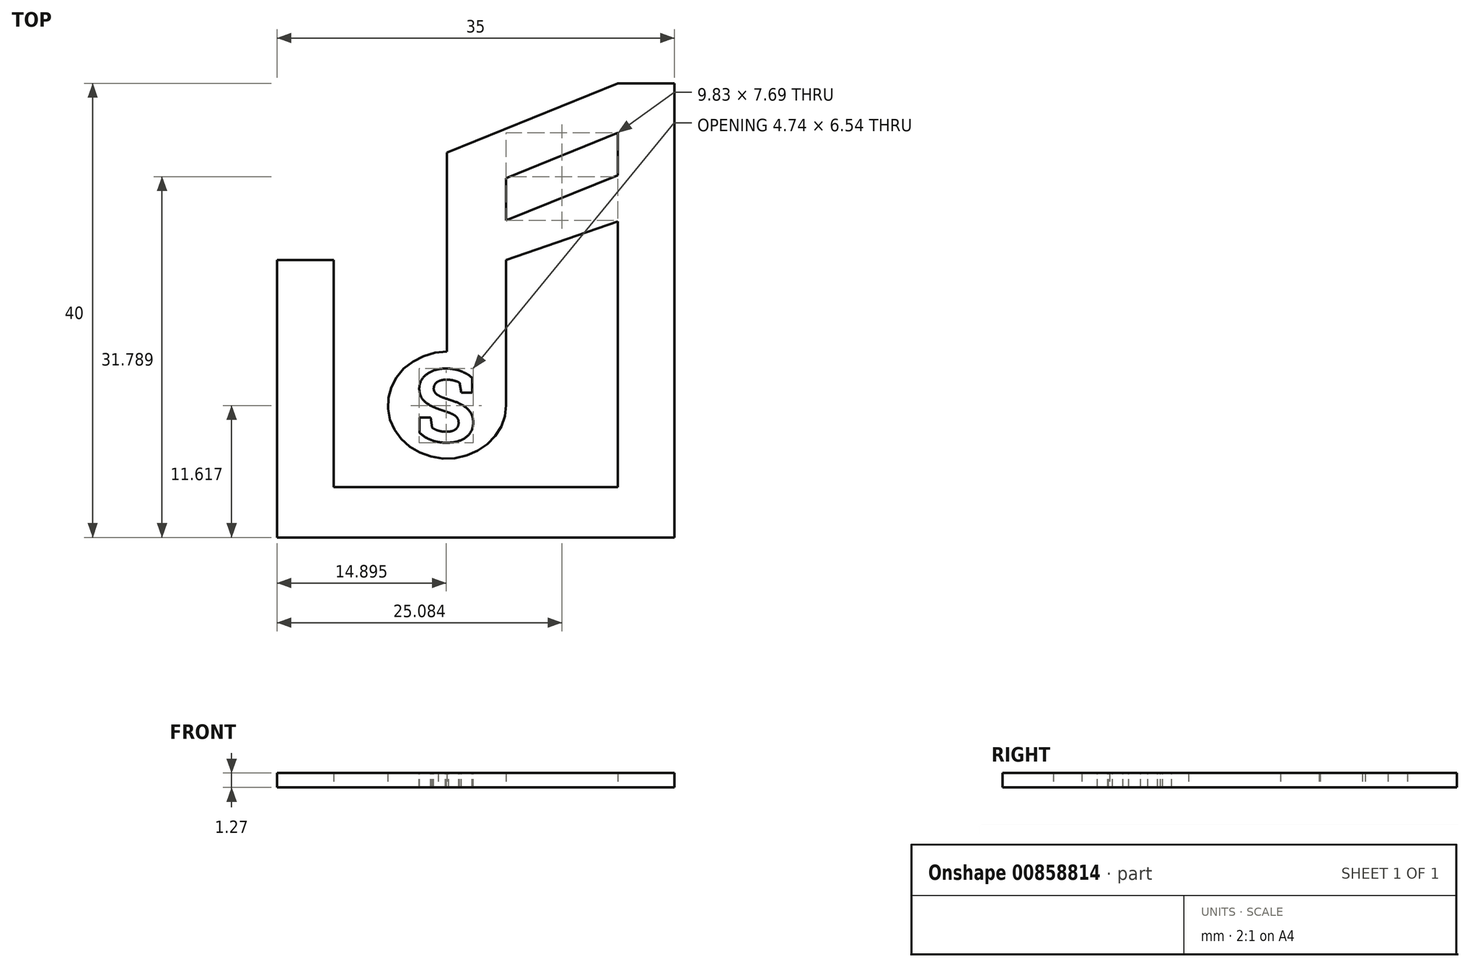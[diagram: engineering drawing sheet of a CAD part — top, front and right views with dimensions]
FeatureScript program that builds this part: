
annotation { "Feature Type Name" : "Feature", "Feature Type Description" : "" }
export const myFeature = defineFeature(function(context is Context, id is Id, definition is map)
    precondition{}
    {
        {
            var Q0;
            Q0=qCreatedBy(makeId("Top.planeOp"),FACE);
            var sketch = newSketch(context, id + "F0", { "sketchPlane" : qUnion([Q0])});
            skLineSegment(sketch, "E0.top", {"start": v(17.5, -24.45) * mm, "end": v(-17.5, -24.45) * mm});
            skLineSegment(sketch, "E0.left", {"start": v(17.5, 15.55) * mm, "end": v(17.5, -24.45) * mm});
            skLineSegment(sketch, "E0.right", {"start": v(-17.5, 0) * mm, "end": v(-17.5, -24.45) * mm});
            skPoint(sketch, "E0.middle", {"position": v(0, 0) * mm});
            skLineSegment(sketch, "E1.top", {"start": v(12.5, -20) * mm, "end": v(-12.5, -20) * mm});
            skLineSegment(sketch, "E1.right", {"start": v(-12.5, 0) * mm, "end": v(-12.5, -20) * mm});
            skLineSegment(sketch, "E2", {"start": v(-2.54, -8.08) * mm, "end": v(-2.54, 9.47) * mm});
            skLineSegment(sketch, "E3", {"start": v(-2.54, 9.47) * mm, "end": v(12.5, 15.55) * mm});
            skLineSegment(sketch, "E4", {"start": v(12.5, 11.19) * mm, "end": v(2.67, 7.21) * mm});
            skLineSegment(sketch, "E5", {"start": v(2.67, 7.21) * mm, "end": v(2.67, 3.5) * mm});
            skEllipticalArc(sketch, "E6", {});
            skLineSegment(sketch, "E7", {"start": v(2.67, 3.5) * mm, "end": v(12.5, 7.47) * mm});
            skLineSegment(sketch, "E8", {"start": v(12.5, 3.4) * mm, "end": v(2.67, 0) * mm});
            skLineSegment(sketch, "E9.trimOffspring", {"start": v(2.67, 0) * mm, "end": v(2.67, -12.8) * mm});
            skLineSegment(sketch, "E10.trimOffspring", {"start": v(12.5, 11.19) * mm, "end": v(12.5, 7.47) * mm});
            skLineSegment(sketch, "E11.trimOffspring", {"start": v(12.5, 3.4) * mm, "end": v(12.5, -20) * mm});
            skPoint(sketch, "E12.middle", {"position": v(-15, 18.05) * mm});
            skPoint(sketch, "E13.MirrorCS.end.orphan", {"position": v(17.5, 16.1) * mm});
            skPoint(sketch, "E13.MirrorCS.start.orphan", {"position": v(12.5, 15.55) * mm});
            skLineSegment(sketch, "E14", {"start": v(-12.5, 0) * mm, "end": v(-17.5, 0) * mm});
            skPoint(sketch, "E15.orphan", {"position": v(-17.5, 16.1) * mm});
            skPoint(sketch, "E12.right.start.orphan", {"position": v(-17.5, 15.55) * mm});
            skPoint(sketch, "E12.top.end.orphan", {"position": v(-17.5, 20.55) * mm});
            skPoint(sketch, "E12.left.end.orphan", {"position": v(-12.5, 20.55) * mm});
            skPoint(sketch, "E12.left.start.orphan", {"position": v(-12.5, 15.55) * mm});
            skLineSegment(sketch, "E16", {"start": v(12.5, 15.55) * mm, "end": v(17.5, 15.55) * mm});
            skPoint(sketch, "E17.MirrorCS.end.orphan", {"position": v(12.5, 20.55) * mm});
            skPoint(sketch, "E18.MirrorCS.end.orphan", {"position": v(17.5, 20.55) * mm});
            skPoint(sketch, "E19.MirrorCS.start.orphan", {"position": v(17.5, 15.55) * mm});
            const initialGuessF0  = {"E6": [-0.00254, -0.012792111374437809, -1, 0, 0.005207451277375222, 0.004707982582969735, 4.71238898038469, 3.141592653589793]};
            skSetInitialGuess(sketch, initialGuessF0);
            skSolve(sketch);
        }
        {
            var Q0;
            Q0=makeQuery(id+"F0.imprint","IMPRINT",FACE,{"disambiguationData":[TD([[makeQuery(id+"F0.imprint","IMPRINT",EDGE,{"derivedFrom":sQuery(id+"F0.wireOp",EDGE,"E0.top")}),-1.0]])]});
            var Q1;
            {var subQ0=sQuery(id+"F0.wireOp",EDGE,"E6");var subQ1=makeQuery(id+"F0.imprint","INTERSECT",VERTEX,{"derivedFrom":[sQuery(id+"F0.wireOp",EDGE,"E2"),subQ0]});Q1=makeQuery(id+"F0.imprint","IMPRINT",FACE,{"disambiguationData":[TD([[makeQuery(id+"F0.imprint","IMPRINT",EDGE,{"disambiguationData":[TD([[subQ1,1.0]])],"derivedFrom":subQ0}),1.0]])]});}
            extrude(context, id + "F1", {"entities" : qUnion([Q0, Q1]), "depth" : 1.27 * mm, "offsetDistance" : 25.4 * mm});
        }
        {
            var Q0;
            Q0=makeQuery(id+"F1.opExtrude","CAP_FACE",FACE,{"disambiguationData":[OSD([sQuery(id+"F0.wireOp",EDGE,"E0.top"),sQuery(id+"F0.wireOp",EDGE,"E0.left"),sQuery(id+"F0.wireOp",EDGE,"E0.right"),sQuery(id+"F0.wireOp",EDGE,"E1.top"),sQuery(id+"F0.wireOp",EDGE,"E1.right"),sQuery(id+"F0.wireOp",EDGE,"E2"),sQuery(id+"F0.wireOp",EDGE,"E3"),sQuery(id+"F0.wireOp",EDGE,"E4"),sQuery(id+"F0.wireOp",EDGE,"E5"),sQuery(id+"F0.wireOp",EDGE,"E6"),sQuery(id+"F0.wireOp",EDGE,"E7"),sQuery(id+"F0.wireOp",EDGE,"E8"),sQuery(id+"F0.wireOp",EDGE,"E9.trimOffspring"),sQuery(id+"F0.wireOp",EDGE,"E10.trimOffspring"),sQuery(id+"F0.wireOp",EDGE,"E11.trimOffspring"),sQuery(id+"F0.wireOp",EDGE,"E14"),sQuery(id+"F0.wireOp",EDGE,"E16")])],"isStart":false});
            var sketch = newSketch(context, id + "F2", { "sketchPlane" : qUnion([Q0])});
            skText(sketch, "E20", { "text": "S", "fontName": "RobotoSlab-Bold.ttf"});
            skPoint(sketch, "E21", {"position": v(-2.54, -12.8) * mm});
            const initialGuessF2  = {"E20": [-0.0054, -0.01601, 1, 0, 0.00644]};
            skSetInitialGuess(sketch, initialGuessF2);
            skSolve(sketch);
        }
        {
            var Q0;
            Q0=makeQuery(id+"F2.imprint","IMPRINT",FACE,{"disambiguationData":[TD([[makeQuery(id+"F2.imprint","IMPRINT",EDGE,{"derivedFrom":sQuery(id+"F2.wireOp",EDGE,"E20.sketch_text.stroke-16")}),-1.0]])]});
            var Q1;
            Q1=makeQuery(id+"F2.imprint","IMPRINT",FACE,{"disambiguationData":[TD([[makeQuery(id+"F2.imprint","IMPRINT",EDGE,{"derivedFrom":sQuery(id+"F2.wireOp",EDGE,"E20.sketch_text.stroke-0")}),-1.0]])]});
            extrude(context, id + "F3", {"entities" : qUnion([Q0, Q1]), "operationType" : NewBodyOperationType.REMOVE, "oppositeDirection" : true, "depth" : 25.4 * mm, "offsetDistance" : 25.4 * mm});
        }
    });
